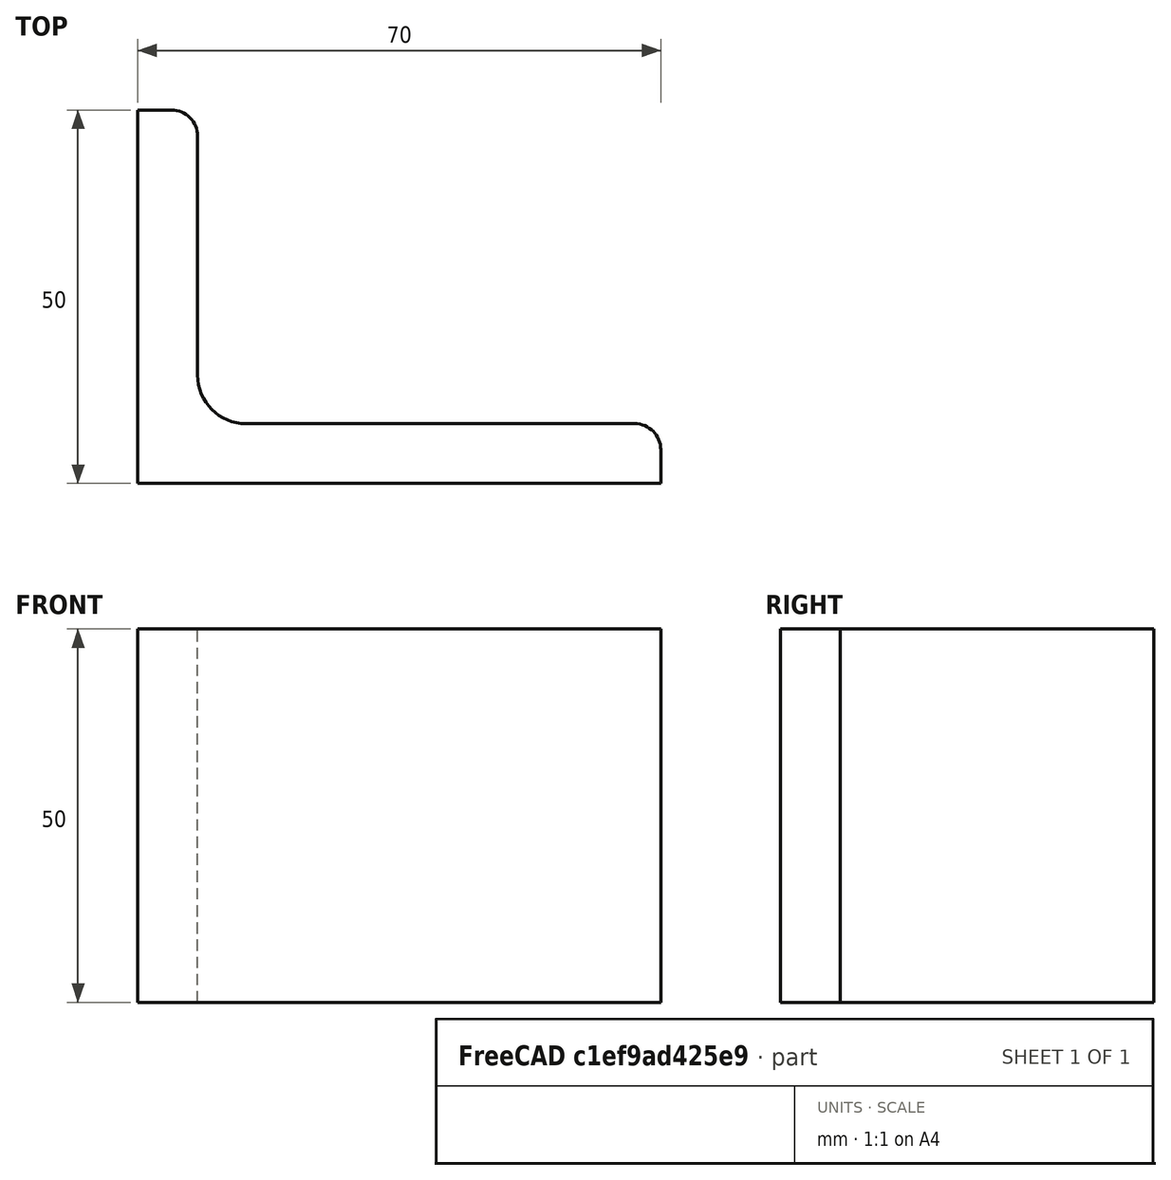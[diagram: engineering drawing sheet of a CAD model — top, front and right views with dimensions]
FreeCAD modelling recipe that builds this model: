
FCSTD DOCUMENT  (FreeCAD 0.15R4671 (Git))
Label: Angle Bar 70x50x8 EN10056 S235JR
License: All rights reserved
LicenseURL: http://en.wikipedia.org/wiki/All_rights_reserved
objects: Sketcher::SketchObject×1, Part::Extrusion×1
note: 2 computed .brp shape members not serialized (recipe doc carries the construction recipe); baked Part::Feature solids carry a one-line shape summary decoded from their .brp

FEATURE [Sketcher::SketchObject] Sketch
  sketch-geometry (9):
    g0: LineSegment StartX=0 StartY=0 StartZ=0 EndX=70 EndY=0 EndZ=0
    g1: LineSegment StartX=70 StartY=0 StartZ=0 EndX=70 EndY=4.5 EndZ=0
    g2: LineSegment StartX=66.5 StartY=8 StartZ=0 EndX=14.5 EndY=8 EndZ=0
    g3: LineSegment StartX=0 StartY=0 StartZ=0 EndX=0 EndY=50 EndZ=0
    g4: LineSegment StartX=0 StartY=50 StartZ=0 EndX=4.5 EndY=50 EndZ=0
    g5: LineSegment StartX=8 StartY=46.5 StartZ=0 EndX=8 EndY=14.5 EndZ=0
    g6: ArcOfCircle CenterX=14.5 CenterY=14.5 CenterZ=0 NormalX=0 NormalY=0 NormalZ=1 Radius=6.5 StartAngle=3.14159 EndAngle=4.71239
    g7: ArcOfCircle CenterX=4.5 CenterY=46.5 CenterZ=0 NormalX=0 NormalY=0 NormalZ=1 Radius=3.5 StartAngle=0 EndAngle=1.5708
    g8: ArcOfCircle CenterX=66.5 CenterY=4.5 CenterZ=0 NormalX=0 NormalY=0 NormalZ=1 Radius=3.5 StartAngle=0 EndAngle=1.5708
  constraints (23):
    c: Coincident(g0,g-1)
    c: Horizontal(g0)
    c: Coincident(g1,g0)
    c: Vertical(g1)
    c: Horizontal(g2)
    c: Coincident(g3,g-1)
    c: Vertical(g3)
    c: Coincident(g4,g3)
    c: Horizontal(g4)
    c: Vertical(g5)
    c: Tangent(g5,g6) = -1.5708
    c: Tangent(g2,g6) = 1.5708
    c: Tangent(g4,g7) = 1.5708
    c: Tangent(g5,g7) = 1.5708
    c: Tangent(g2,g8) = -1.5708
    c: Tangent(g1,g8) = -1.5708
    c: DistanceX(g0) = 70
    c: DistanceY(g3) = 50
    c: DistanceY(g0,g2) = 8
    c: DistanceX(g3,g5) = 8
    c: Radius(g6) = 6.5
    c: Radius(g8) = 3.5
    c: Radius(g7) = 3.5
FEATURE [Part::Extrusion] Extrude  label="Angle Bar 70x50x8 EN10056 S235JR"
  Base = -> Sketch
  Dir = (0,0,50)
  Solid = true
